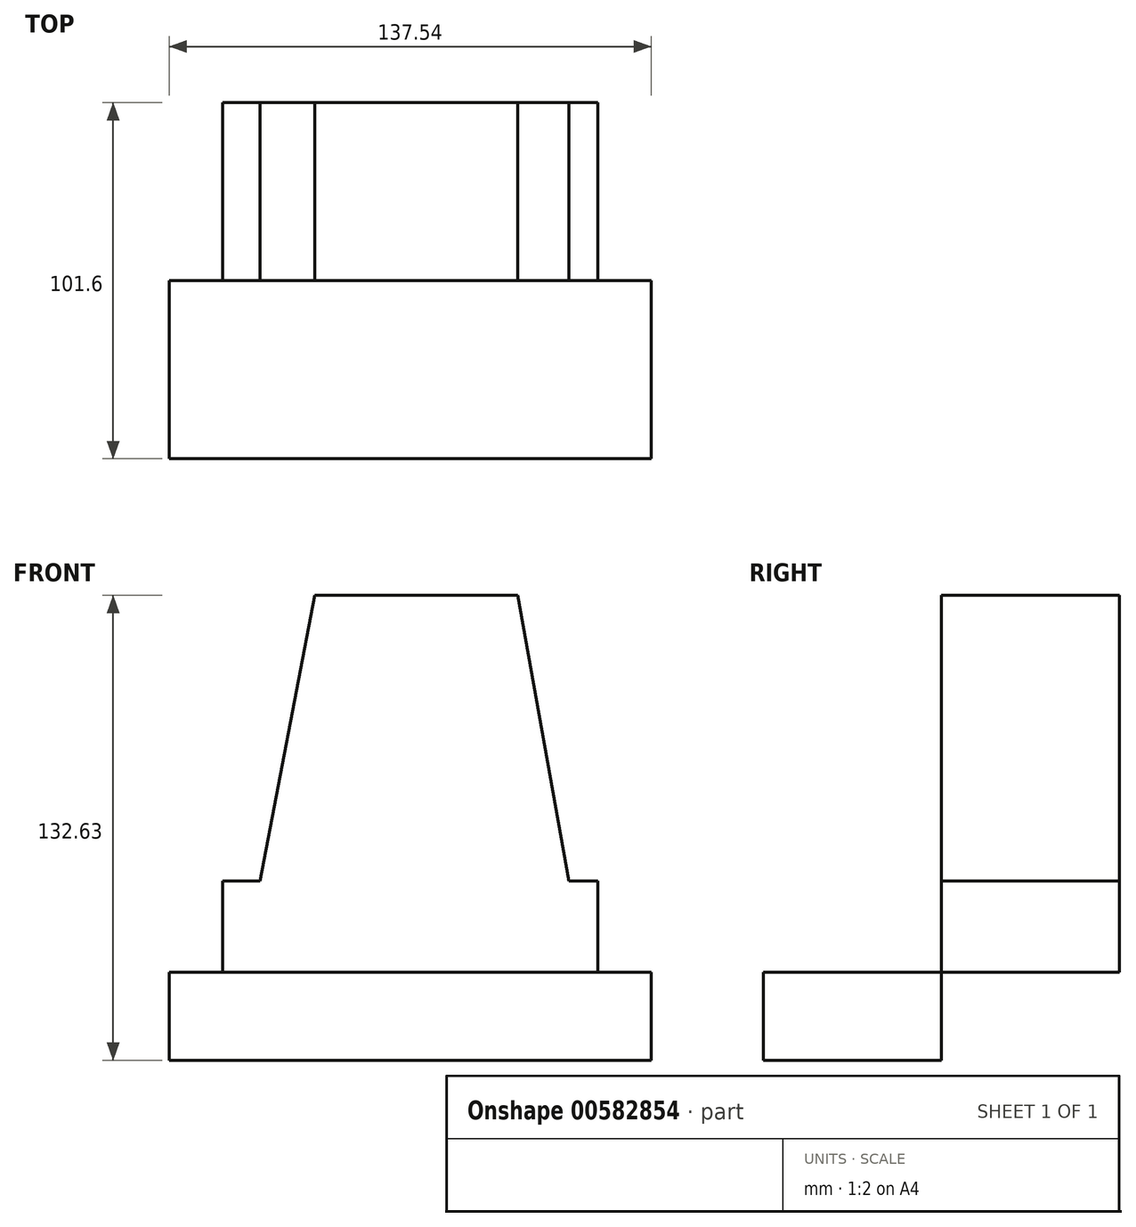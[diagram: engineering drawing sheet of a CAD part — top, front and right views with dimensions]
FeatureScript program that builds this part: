
annotation { "Feature Type Name" : "Feature", "Feature Type Description" : "" }
export const myFeature = defineFeature(function(context is Context, id is Id, definition is map)
    precondition{}
    {
        {
            var Q0;
            Q0=qCreatedBy(makeId("Front.planeOp"),FACE);
            var sketch = newSketch(context, id + "F0", { "sketchPlane" : qUnion([Q0])});
            skLineSegment(sketch, "E0.bottom", {"start": v(-130.63, 26.05) * mm, "end": v(-23.57, 26.05) * mm});
            skLineSegment(sketch, "E0.top", {"start": v(-130.63, 0) * mm, "end": v(-23.57, 0) * mm});
            skLineSegment(sketch, "E0.left", {"start": v(-130.63, 26.05) * mm, "end": v(-130.63, 0) * mm});
            skLineSegment(sketch, "E0.right", {"start": v(-23.57, 26.05) * mm, "end": v(-23.57, 0) * mm});
            skLineSegment(sketch, "E1", {"start": v(-120.02, 26.05) * mm, "end": v(-104.4, 107.53) * mm});
            skLineSegment(sketch, "E2", {"start": v(-104.4, 107.53) * mm, "end": v(-46.48, 107.53) * mm});
            skLineSegment(sketch, "E3", {"start": v(-31.88, 26.05) * mm, "end": v(-46.48, 107.53) * mm});
            skSolve(sketch);
        }
        {
            var Q0;
            Q0=makeQuery(id+"F0.imprint","IMPRINT",FACE,{"disambiguationData":[TD([[makeQuery(id+"F0.imprint","IMPRINT",EDGE,{"derivedFrom":sQuery(id+"F0.wireOp",EDGE,"E0.top")}),1.0]])]});
            var Q1;
            {var subQ0=sQuery(id+"F0.wireOp",EDGE,"E1");Q1=makeQuery(id+"F0.imprint","IMPRINT",FACE,{"disambiguationData":[TD([[makeQuery(id+"F0.imprint","IMPRINT",EDGE,{"derivedFrom":subQ0}),-1.0]])]});}
            extrude(context, id + "F1", {"entities" : qUnion([Q0, Q1]), "depth" : 50.8 * mm, "offsetDistance" : 25.4 * mm});
        }
        {
            var Q0;
            Q0=makeQuery(id+"F1.opExtrude","CAP_FACE",FACE,{"disambiguationData":[OSD([sQuery(id+"F0.wireOp",EDGE,"E0.bottom"),sQuery(id+"F0.wireOp",EDGE,"E0.top"),sQuery(id+"F0.wireOp",EDGE,"E0.left"),sQuery(id+"F0.wireOp",EDGE,"E0.right"),sQuery(id+"F0.wireOp",EDGE,"E1"),sQuery(id+"F0.wireOp",EDGE,"E2"),sQuery(id+"F0.wireOp",EDGE,"E3")])],"isStart":false});
            var sketch = newSketch(context, id + "F2", { "sketchPlane" : qUnion([Q0])});
            skLineSegment(sketch, "E4", {"start": v(-130.63, 0) * mm, "end": v(-145.87, 0) * mm});
            skLineSegment(sketch, "E5", {"start": v(-23.57, 0) * mm, "end": v(-8.33, 0) * mm});
            skLineSegment(sketch, "E6", {"start": v(-145.87, 0) * mm, "end": v(-145.87, -25.1) * mm});
            skLineSegment(sketch, "E7", {"start": v(-8.33, 0) * mm, "end": v(-8.33, -25.1) * mm});
            skLineSegment(sketch, "E8", {"start": v(-145.87, -25.1) * mm, "end": v(-8.33, -25.1) * mm});
            skSolve(sketch);
        }
        {
            var Q0;
            Q0 = qSketchRegion(id + "F2", true);
            var Q1;
            Q1=makeQuery(id+"F2.imprint","IMPRINT",FACE,{"disambiguationData":[TD([[makeQuery(id+"F2.imprint","IMPRINT",EDGE,{"derivedFrom":sQuery(id+"F2.wireOp",EDGE,"E4")}),1.0]])]});
            extrude(context, id + "F3", {"entities" : qUnion([Q0, Q1]), "depth" : 25.4 * mm, "offsetDistance" : 25.4 * mm});
        }
        {
            var Q0;
            Q0=makeQuery(id+"F1.opExtrude","CAP_FACE",FACE,{"disambiguationData":[OSD([sQuery(id+"F0.wireOp",EDGE,"E0.bottom"),sQuery(id+"F0.wireOp",EDGE,"E0.top"),sQuery(id+"F0.wireOp",EDGE,"E0.left"),sQuery(id+"F0.wireOp",EDGE,"E0.right"),sQuery(id+"F0.wireOp",EDGE,"E1"),sQuery(id+"F0.wireOp",EDGE,"E2"),sQuery(id+"F0.wireOp",EDGE,"E3")])],"isStart":false});
            var sketch = newSketch(context, id + "F4", { "sketchPlane" : qUnion([Q0])});
            skSolve(sketch);
        }
        {
            var Q0;
            Q0=makeQuery(id+"F3.opExtrude","CAP_FACE",FACE,{"disambiguationData":[OSD([sQuery(id+"F0.wireOp",EDGE,"E0.top"),sQuery(id+"F2.wireOp",EDGE,"E4"),sQuery(id+"F2.wireOp",EDGE,"E5"),sQuery(id+"F2.wireOp",EDGE,"E6"),sQuery(id+"F2.wireOp",EDGE,"E7"),sQuery(id+"F2.wireOp",EDGE,"E8")])],"isStart":false});
            var Q1;
            Q1 = qSketchRegion(id + "F4", true);
            extrude(context, id + "F5", {"entities" : qUnion([Q0, Q1]), "operationType" : NewBodyOperationType.ADD, "depth" : 25.4 * mm, "offsetDistance" : 25.4 * mm});
        }
    });
